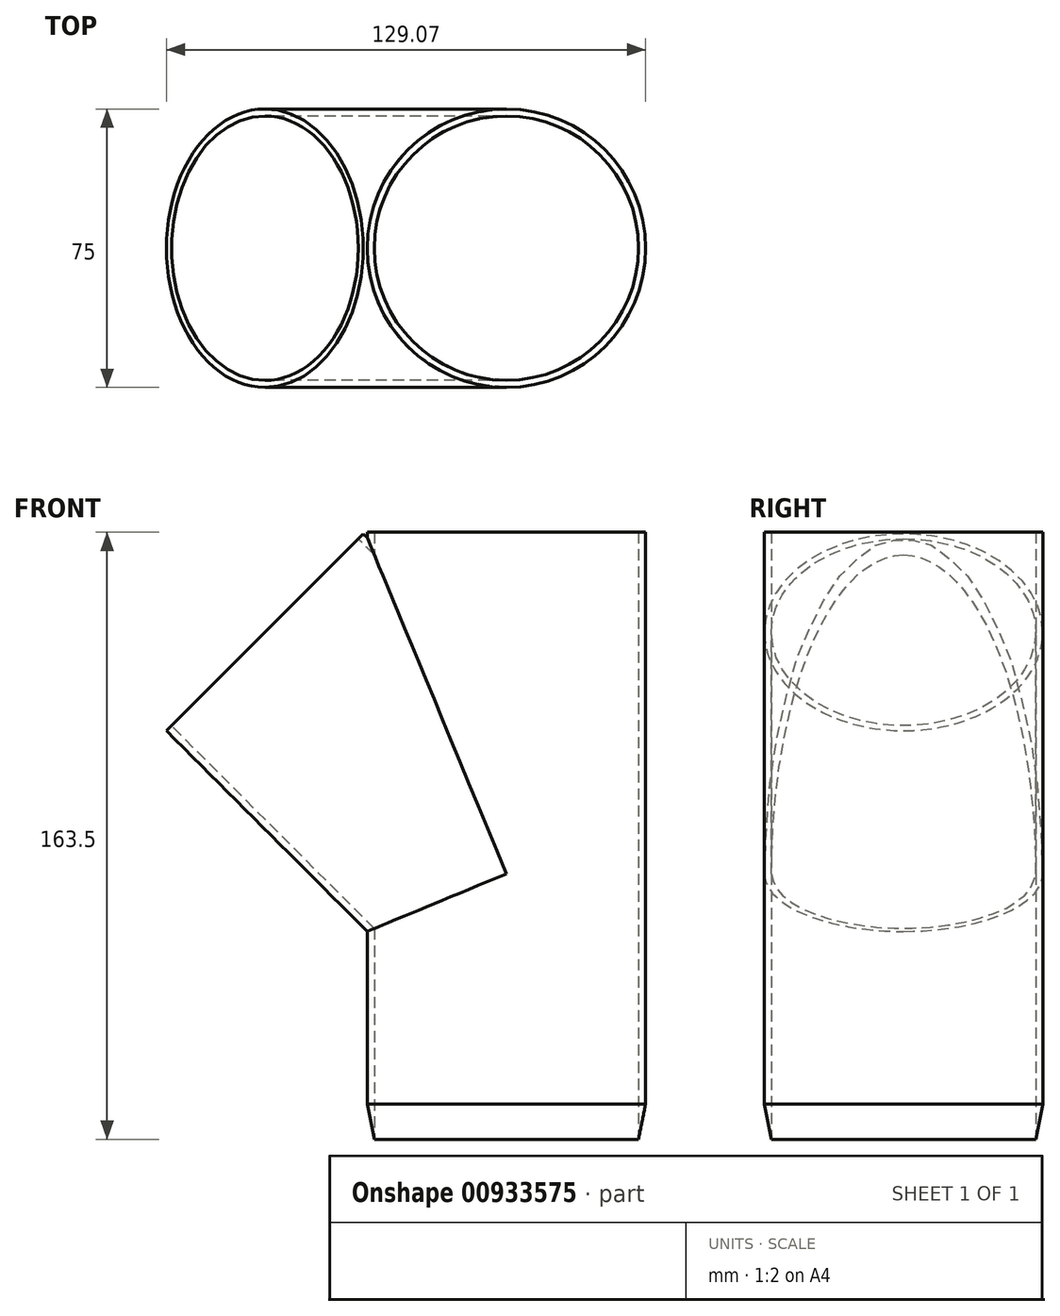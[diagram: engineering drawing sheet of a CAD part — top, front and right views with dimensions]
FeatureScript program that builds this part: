
annotation { "Feature Type Name" : "Feature", "Feature Type Description" : "" }
export const myFeature = defineFeature(function(context is Context, id is Id, definition is map)
    precondition{}
    {
        {
            var Q0;
            Q0=qCreatedBy(makeId("Top.planeOp"),FACE);
            var sketch = newSketch(context, id + "F0", { "sketchPlane" : qUnion([Q0])});
            skCircle(sketch, "E0", {"center": v(0, 0) * mm, "radius": 37.5 * mm});
            skSolve(sketch);
        }
        {
            var Q0;
            Q0 = qSketchRegion(id + "F0", true);
            extrude(context, id + "F1", {"entities" : qUnion([Q0]), "depth" : 164 * mm, "offsetDistance" : 25 * mm});
        }
        {
            var Q0;
            Q0=qCreatedBy(makeId("Front.planeOp"),FACE);
            var sketch = newSketch(context, id + "F2", { "sketchPlane" : qUnion([Q0])});
            skLineSegment(sketch, "E1", {"start": v(0, 72) * mm, "end": v(-56.54, 128.54) * mm, "construction": true});
            skLineSegment(sketch, "E2", {"start": v(0, 43.8) * mm, "end": v(0, 120.58) * mm, "construction": true});
            skLineSegment(sketch, "E3", {"start": v(-26.52, 45.48) * mm, "end": v(-91.57, 110.54) * mm});
            skLineSegment(sketch, "E4", {"start": v(0, 72) * mm, "end": v(-27.56, 44.44) * mm, "construction": true});
            skLineSegment(sketch, "E5", {"start": v(-1.41, 73.41) * mm, "end": v(0, 72) * mm});
            skLineSegment(sketch, "E6", {"start": v(-26.52, 45.48) * mm, "end": v(0, 72) * mm});
            skLineSegment(sketch, "E7", {"start": v(-91.57, 110.54) * mm, "end": v(-65.05, 137.05) * mm});
            skLineSegment(sketch, "E8", {"start": v(-65.05, 137.05) * mm, "end": v(0, 72) * mm});
            skSolve(sketch);
        }
        {
            var Q0;
            Q0 = qSketchRegion(id + "F2", true);
            var Q1;
            Q1=sQuery(id+"F2.wireOp",EDGE,"E1");
            revolve(context, id + "F3", {"operationType" : NewBodyOperationType.ADD, "surfaceOperationType" : NewSurfaceOperationType.NEW, "entities" : qUnion([Q0]), "axis" : qUnion([Q1]), "revolveType" : RevolveType.FULL});
        }
        {
            var Q0;
            Q0=qCreatedBy(makeId("Front.planeOp"),FACE);
            var sketch = newSketch(context, id + "F4", { "sketchPlane" : qUnion([Q0])});
            skLineSegment(sketch, "E9", {"start": v(37.5, 0) * mm, "end": v(35.5, 0) * mm});
            skLineSegment(sketch, "E10", {"start": v(35.5, 0) * mm, "end": v(37.5, 10) * mm});
            skLineSegment(sketch, "E11", {"start": v(37.5, 10) * mm, "end": v(37.5, 0) * mm});
            skLineSegment(sketch, "E12", {"start": v(0, -22.9) * mm, "end": v(0, 22.96) * mm, "construction": true});
            skSolve(sketch);
        }
        {
            var Q0;
            Q0 = qSketchRegion(id + "F4", true);
            var Q1;
            Q1=sQuery(id+"F4.wireOp",EDGE,"E12");
            revolve(context, id + "F5", {"operationType" : NewBodyOperationType.REMOVE, "surfaceOperationType" : NewSurfaceOperationType.NEW, "entities" : qUnion([Q0]), "axis" : qUnion([Q1]), "revolveType" : RevolveType.FULL, "oppositeDirection" : true});
        }
        {
            var Q0;
            Q0=makeQuery(id+"F1.opExtrude","CAP_FACE",FACE,{"disambiguationData":[OSD([sQuery(id+"F0.wireOp",EDGE,"E0")])],"isStart":true});
            var sketch = newSketch(context, id + "F6", { "sketchPlane" : qUnion([Q0])});
            skCircle(sketch, "E13", {"center": v(0, 0) * mm, "radius": 35.6 * mm});
            skSolve(sketch);
        }
        {
            var Q0;
            Q0 = qSketchRegion(id + "F6", true);
            extrude(context, id + "F7", {"entities" : qUnion([Q0]), "operationType" : NewBodyOperationType.REMOVE, "endBound" : BoundingType.THROUGH_ALL, "oppositeDirection" : true, "depth" : 25 * mm, "offsetDistance" : 25 * mm});
        }
        {
            var Q0;
            Q0=makeQuery(id+"F3.opRevolve","SWEPT_FACE",FACE,{"disambiguationData":[OSD([sQuery(id+"F2.wireOp",EDGE,"E7")])]});
            var sketch = newSketch(context, id + "F8", { "sketchPlane" : qUnion([Q0])});
            skCircle(sketch, "E14", {"center": v(0, 50.91) * mm, "radius": 35.6 * mm});
            skSolve(sketch);
        }
        {
            var Q0;
            Q0 = qSketchRegion(id + "F8", true);
            extrude(context, id + "F9", {"entities" : qUnion([Q0]), "operationType" : NewBodyOperationType.REMOVE, "oppositeDirection" : true, "depth" : 92 * mm, "offsetDistance" : 25 * mm});
        }
    });
